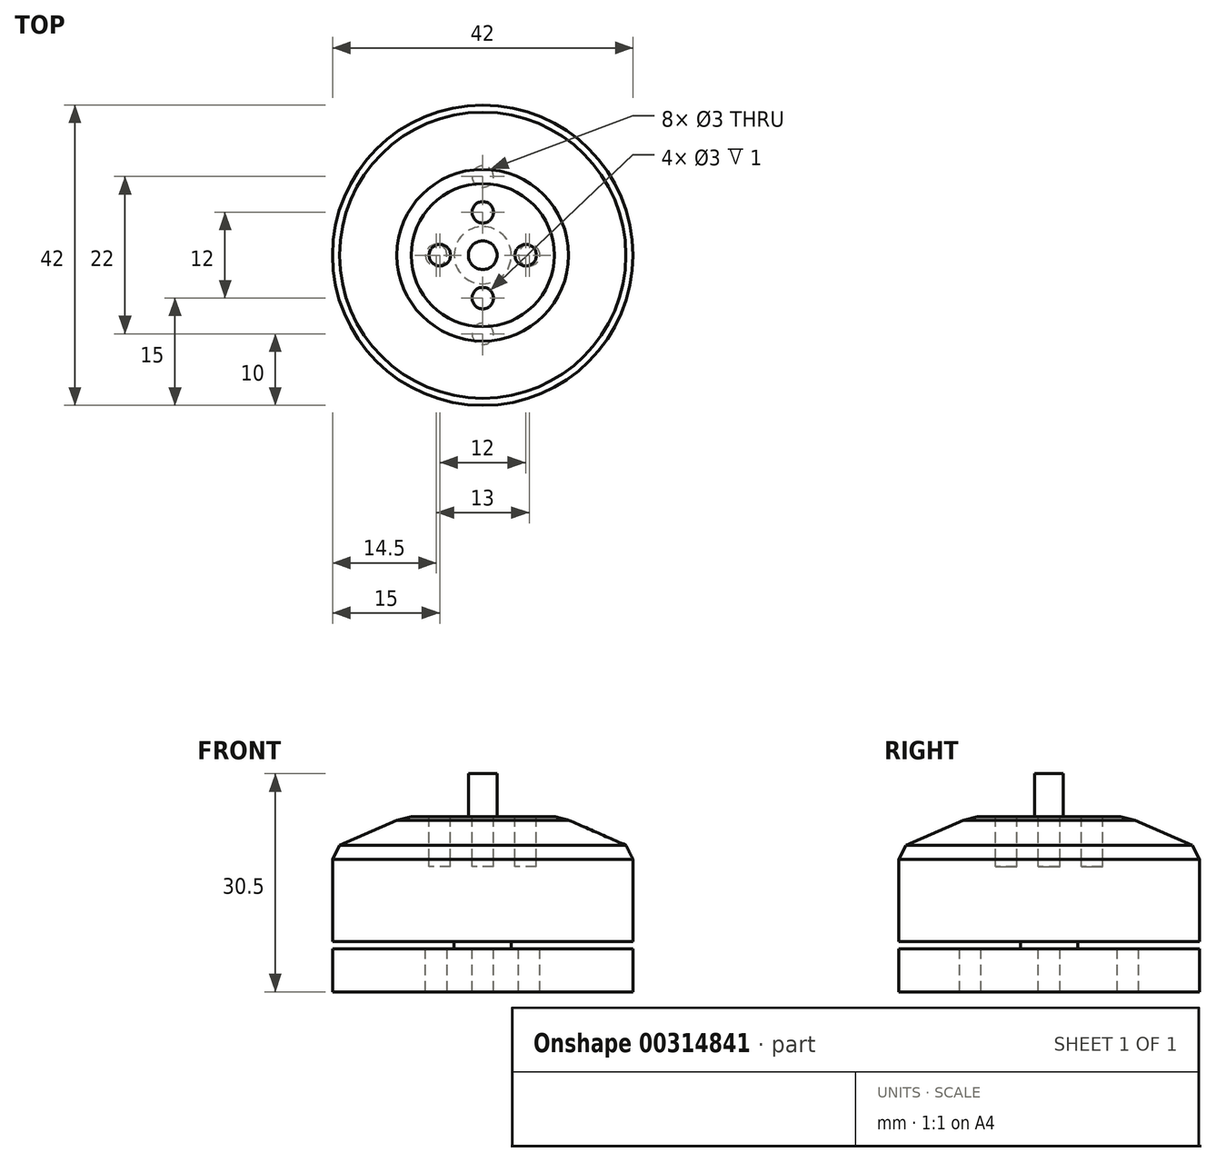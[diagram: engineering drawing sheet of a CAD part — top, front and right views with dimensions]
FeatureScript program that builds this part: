
annotation { "Feature Type Name" : "Feature", "Feature Type Description" : "" }
export const myFeature = defineFeature(function(context is Context, id is Id, definition is map)
    precondition{}
    {
        {
            var Q0;
            Q0=qCreatedBy(makeId("Top.planeOp"),FACE);
            var sketch = newSketch(context, id + "F0", { "sketchPlane" : qUnion([Q0])});
            skCircle(sketch, "E0", {"center": v(0, 0) * mm, "radius": 21 * mm});
            skSolve(sketch);
        }
        {
            var Q0;
            Q0=makeQuery(id+"F0.imprint","IMPRINT",FACE,{"disambiguationData":[TD([[makeQuery(id+"F0.imprint","IMPRINT",EDGE,{"derivedFrom":sQuery(id+"F0.wireOp",EDGE,"E0")}),1.0]])]});
            var Q1;
            Q1=sQuery(id+"F0.wireOp",EDGE,"E0");
            extrude(context, id + "F1", {"entities" : qUnion([Q0]), "surfaceEntities" : qUnion([Q1]), "depth" : 11.5 * mm});
        }
        {
            var Q0;
            Q0=qCreatedBy(makeId("Front.planeOp"),FACE);
            var sketch = newSketch(context, id + "F2", { "sketchPlane" : qUnion([Q0])});
            skLineSegment(sketch, "E1.0", {"start": v(-21, 11.5) * mm, "end": v(0, 11.5) * mm});
            skLineSegment(sketch, "E2", {"start": v(-12, 17) * mm, "end": v(-20, 13.5) * mm});
            skLineSegment(sketch, "E3", {"start": v(-21, 11.5) * mm, "end": v(-20, 13.5) * mm});
            skLineSegment(sketch, "E4", {"start": v(-12, 17) * mm, "end": v(-10, 17.5) * mm});
            skLineSegment(sketch, "E5", {"start": v(-10, 17.5) * mm, "end": v(0, 17.5) * mm});
            skLineSegment(sketch, "E6", {"start": v(0, 17.5) * mm, "end": v(0, 11.5) * mm});
            skPoint(sketch, "E7.orphan", {"position": v(21, 11.5) * mm});
            skSolve(sketch);
        }
        {
            var Q0;
            Q0 = qSketchRegion(id + "F2", true);
            var Q1;
            Q1=makeQuery(id+"F1.opExtrude","SWEPT_FACE",FACE,{"disambiguationData":[OSD([sQuery(id+"F0.wireOp",EDGE,"E0")])]});
            revolve(context, id + "F3", {"entities" : qUnion([Q0]), "axis" : qUnion([Q1]), "revolveType" : RevolveType.FULL});
        }
        {
            var Q0;
            Q0=makeQuery(id+"F3.opRevolve","SWEPT_FACE",FACE,{"disambiguationData":[OSD([sQuery(id+"F2.wireOp",EDGE,"E5")])]});
            var sketch = newSketch(context, id + "F4", { "sketchPlane" : qUnion([Q0])});
            skCircle(sketch, "E8", {"center": v(0, 0) * mm, "radius": 2 * mm});
            skCircle(sketch, "E9", {"center": v(0, 6) * mm, "radius": 1.5 * mm});
            skCircle(sketch, "E10.1.0", {"center": v(-6, 0) * mm, "radius": 1.5 * mm});
            skCircle(sketch, "E10.2.0", {"center": v(0, -6) * mm, "radius": 1.5 * mm});
            skCircle(sketch, "E11.1.3.0", {"center": v(6, 0) * mm, "radius": 1.5 * mm});
            skSolve(sketch);
        }
        {
            var Q0;
            Q0=makeQuery(id+"F4.imprint","IMPRINT",FACE,{"disambiguationData":[TD([[makeQuery(id+"F4.imprint","IMPRINT",EDGE,{"derivedFrom":sQuery(id+"F4.wireOp",EDGE,"E8")}),1.0]])]});
            extrude(context, id + "F5", {"entities" : qUnion([Q0]), "operationType" : NewBodyOperationType.ADD, "depth" : 6 * mm});
        }
        {
            var Q0;
            Q0=makeQuery(id+"F4.imprint","IMPRINT",FACE,{"disambiguationData":[TD([[makeQuery(id+"F4.imprint","IMPRINT",EDGE,{"derivedFrom":sQuery(id+"F4.wireOp",EDGE,"E9")}),1.0]])]});
            var Q1;
            Q1=makeQuery(id+"F4.imprint","IMPRINT",FACE,{"disambiguationData":[TD([[makeQuery(id+"F4.imprint","IMPRINT",EDGE,{"derivedFrom":sQuery(id+"F4.wireOp",EDGE,"E10.1.0")}),1.0]])]});
            var Q2;
            Q2=makeQuery(id+"F4.imprint","IMPRINT",FACE,{"disambiguationData":[TD([[makeQuery(id+"F4.imprint","IMPRINT",EDGE,{"derivedFrom":sQuery(id+"F4.wireOp",EDGE,"E10.2.0")}),1.0]])]});
            var Q3;
            Q3=makeQuery(id+"F4.imprint","IMPRINT",FACE,{"disambiguationData":[TD([[makeQuery(id+"F4.imprint","IMPRINT",EDGE,{"derivedFrom":sQuery(id+"F4.wireOp",EDGE,"E11.1.3.0")}),1.0]])]});
            extrude(context, id + "F6", {"entities" : qUnion([Q0, Q1, Q2, Q3]), "operationType" : NewBodyOperationType.REMOVE, "oppositeDirection" : true, "depth" : 7 * mm});
        }
        {
            var Q0;
            Q0=makeQuery(id+"F1.opExtrude","CAP_FACE",FACE,{"disambiguationData":[OSD([sQuery(id+"F0.wireOp",EDGE,"E0")])],"isStart":true});
            cPlane(context, id + "F7", {"entities" : qUnion([Q0]), "cplaneType" : CPlaneType.OFFSET, "offset" : 1 * mm, "width" : 150 * mm, "height" : 150 * mm});
        }
        {
            var Q0;
            Q0=qCreatedBy(id+"F7.planeOp",FACE);
            var sketch = newSketch(context, id + "F8", { "sketchPlane" : qUnion([Q0])});
            skCircle(sketch, "E12.0.0", {"center": v(0, 0) * mm, "radius": 21 * mm});
            skCircle(sketch, "E13", {"center": v(0, 0) * mm, "radius": 12.5 * mm, "construction": true});
            skLineSegment(sketch, "E14", {"start": v(-12.5, 0) * mm, "end": v(0, 0) * mm, "construction": true});
            skLineSegment(sketch, "E15", {"start": v(0, 0) * mm, "end": v(0, -12.5) * mm, "construction": true});
            skLineSegment(sketch, "E16", {"start": v(0, 0) * mm, "end": v(12.5, 0) * mm, "construction": true});
            skLineSegment(sketch, "E17", {"start": v(0, 0) * mm, "end": v(-12.5, 0) * mm, "construction": true});
            skLineSegment(sketch, "E18", {"start": v(0, 0) * mm, "end": v(0, 12.5) * mm, "construction": true});
            skCircle(sketch, "E19", {"center": v(0, 11) * mm, "radius": 1.5 * mm});
            skCircle(sketch, "E20", {"center": v(0, -11) * mm, "radius": 1.5 * mm});
            skCircle(sketch, "E21", {"center": v(0, 0) * mm, "radius": 8 * mm, "construction": true});
            skCircle(sketch, "E22", {"center": v(-6.5, 0) * mm, "radius": 1.5 * mm});
            skCircle(sketch, "E23", {"center": v(6.5, 0) * mm, "radius": 1.5 * mm});
            skCircle(sketch, "E24", {"center": v(0, 0) * mm, "radius": 4 * mm});
            skSolve(sketch);
        }
        {
            var Q0;
            Q0=makeQuery(id+"F8.imprint","IMPRINT",FACE,{"disambiguationData":[TD([[makeQuery(id+"F8.imprint","IMPRINT",EDGE,{"derivedFrom":sQuery(id+"F8.wireOp",EDGE,"E12.0.0")}),1.0]])]});
            var Q1;
            Q1=makeQuery(id+"F8.imprint","IMPRINT",FACE,{"disambiguationData":[TD([[makeQuery(id+"F8.imprint","IMPRINT",EDGE,{"derivedFrom":sQuery(id+"F8.wireOp",EDGE,"E24")}),1.0]])]});
            extrude(context, id + "F9", {"entities" : qUnion([Q0, Q1]), "depth" : 6 * mm});
        }
        {
            var Q0;
            Q0=makeQuery(id+"F8.imprint","IMPRINT",FACE,{"disambiguationData":[TD([[makeQuery(id+"F8.imprint","IMPRINT",EDGE,{"derivedFrom":sQuery(id+"F8.wireOp",EDGE,"E24")}),1.0]])]});
            extrude(context, id + "F10", {"entities" : qUnion([Q0]), "operationType" : NewBodyOperationType.ADD, "oppositeDirection" : true, "depth" : 1 * mm});
        }
    });
